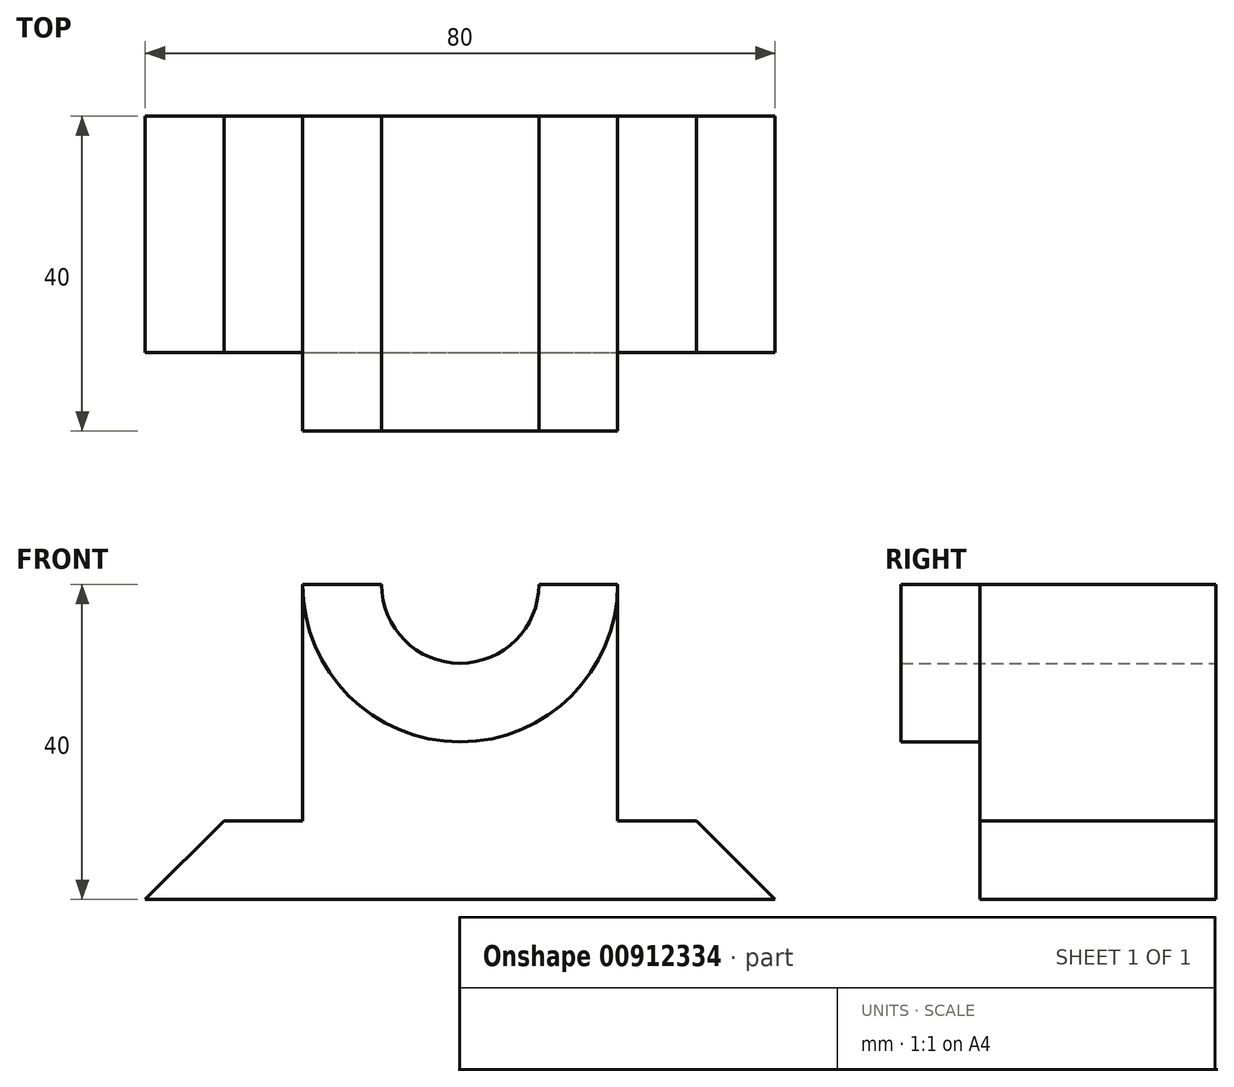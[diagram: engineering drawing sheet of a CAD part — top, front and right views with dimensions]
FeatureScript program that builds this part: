
annotation { "Feature Type Name" : "Feature", "Feature Type Description" : "" }
export const myFeature = defineFeature(function(context is Context, id is Id, definition is map)
    precondition{}
    {
        {
            var Q0;
            Q0=qCreatedBy(makeId("Front.planeOp"),FACE);
            var sketch = newSketch(context, id + "F0", { "sketchPlane" : qUnion([Q0])});
            skLineSegment(sketch, "E0", {"start": v(0, 0) * mm, "end": v(0, 51.5) * mm, "construction": true});
            skLineSegment(sketch, "E1", {"start": v(20, 40) * mm, "end": v(20, 10) * mm});
            skLineSegment(sketch, "E2", {"start": v(20, 10) * mm, "end": v(30, 10) * mm});
            skLineSegment(sketch, "E3", {"start": v(30, 10) * mm, "end": v(40, 0) * mm});
            skLineSegment(sketch, "E4.MirrorCS", {"start": v(-20, 40) * mm, "end": v(-20, 10) * mm});
            skLineSegment(sketch, "E5.MirrorCS", {"start": v(-20, 10) * mm, "end": v(-30, 10) * mm});
            skLineSegment(sketch, "E6.MirrorCS", {"start": v(-30, 10) * mm, "end": v(-40, 0) * mm});
            skLineSegment(sketch, "E7", {"start": v(-40, 0) * mm, "end": v(40, 0) * mm});
            skLineSegment(sketch, "E8", {"start": v(-20, 40) * mm, "end": v(20, 40) * mm});
            skSolve(sketch);
        }
        {
            var Q0;
            Q0=makeQuery(id+"F0.imprint","IMPRINT",FACE,{"disambiguationData":[TD([[makeQuery(id+"F0.imprint","IMPRINT",EDGE,{"derivedFrom":sQuery(id+"F0.wireOp",EDGE,"E1")}),-1.0]])]});
            extrude(context, id + "F1", {"entities" : qUnion([Q0]), "depth" : 30 * mm, "offsetDistance" : 25 * mm});
        }
        {
            var Q0;
            Q0=makeQuery(id+"F1.opExtrude","CAP_FACE",FACE,{"disambiguationData":[OSD([sQuery(id+"F0.wireOp",EDGE,"E1"),sQuery(id+"F0.wireOp",EDGE,"E2"),sQuery(id+"F0.wireOp",EDGE,"E3"),sQuery(id+"F0.wireOp",EDGE,"E4.MirrorCS"),sQuery(id+"F0.wireOp",EDGE,"E5.MirrorCS"),sQuery(id+"F0.wireOp",EDGE,"E6.MirrorCS"),sQuery(id+"F0.wireOp",EDGE,"E7"),sQuery(id+"F0.wireOp",EDGE,"E8")])],"isStart":false});
            var sketch = newSketch(context, id + "F2", { "sketchPlane" : qUnion([Q0])});
            skArc(sketch, "E9", {"start": v(-10, 40) * mm, "mid": v(0, 30) * mm, "end": v(10, 40) * mm});
            skLineSegment(sketch, "E10.0", {"start": v(-20, 40) * mm, "end": v(20, 40) * mm});
            skArc(sketch, "E11", {"start": v(-20, 40) * mm, "mid": v(0, 20) * mm, "end": v(20, 40) * mm});
            skSolve(sketch);
        }
        {
            var Q0;
            {var subQ0=sQuery(id+"F2.wireOp",EDGE,"E9");Q0=makeQuery(id+"F2.imprint","IMPRINT",FACE,{"disambiguationData":[TD([[makeQuery(id+"F2.imprint","IMPRINT",EDGE,{"derivedFrom":subQ0}),-1.0]])]});}
            extrude(context, id + "F3", {"entities" : qUnion([Q0]), "operationType" : NewBodyOperationType.ADD, "depth" : 10 * mm, "offsetDistance" : 25 * mm});
        }
        {
            var Q0;
            {var subQ0=sQuery(id+"F0.wireOp",EDGE,"E8");var subQ1=sQuery(id+"F2.wireOp",EDGE,"E9");var subQ4=sQuery(id+"F0.wireOp",EDGE,"E1");var subQ5=sQuery(id+"F0.wireOp",EDGE,"E4.MirrorCS");Q0=makeQuery(id+"F3.boolean.opBoolean","SPLIT",FACE,{"disambiguationData":[TD([makeQuery(id+"F3.opExtrude","SWEPT_FACE",FACE,{"disambiguationData":[OSD([subQ1])]})])],"derivedFrom":makeQuery(id+"F1.opExtrude","CAP_FACE",FACE,{"disambiguationData":[OSD([subQ4,sQuery(id+"F0.wireOp",EDGE,"E2"),sQuery(id+"F0.wireOp",EDGE,"E3"),subQ5,sQuery(id+"F0.wireOp",EDGE,"E5.MirrorCS"),sQuery(id+"F0.wireOp",EDGE,"E6.MirrorCS"),sQuery(id+"F0.wireOp",EDGE,"E7"),subQ0])],"isStart":false})});}
            extrude(context, id + "F4", {"entities" : qUnion([Q0]), "operationType" : NewBodyOperationType.REMOVE, "endBound" : BoundingType.THROUGH_ALL, "oppositeDirection" : true, "depth" : 25 * mm, "offsetDistance" : 25 * mm});
        }
    });
